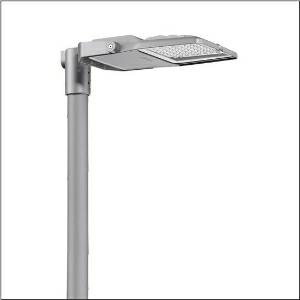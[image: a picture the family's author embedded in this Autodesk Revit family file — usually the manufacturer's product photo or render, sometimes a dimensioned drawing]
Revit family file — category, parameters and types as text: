
# Revit family: floodlight_fl_21_mini___pl33t_5xa7772b4f3a_78ab
name_source: partatom
category: Lighting Fixtures
units: mm (PartAtom-declared; Revit-internal decimal feet)

## family parameters
Cut with Voids When Loaded = No
Host = Face
Light Source = No
Part Type = Normal
Room Calculation Point = No
Round Connector Dimension = Use Diameter
Shared = No

## types (1)
- --- (1 x LED, 6420 lm, 45.5 W, 4000K)
    Apparent Load = 46 VA
    CIE Flux Codes = 26 75 99 100 100
    Color Rendering = 70
    Color Temperature = 4000K
    Default Elevation = 1800 mm
    Description = Floodlight FL 21 mini, floodlight, primary light control with lens, of PMMA, primary optical cover: protective disc, of toughened safety glass, transparent, light distribution: PL33T, light emission: direct distribution, installation type: surface-mounted, LED, High Power LED, rated luminous flux: 6.420lm, luminous efficacy: 141lm/W, light colour: 740, colour temperature: 4000K, control gear: ECG iQ, control: Auto-Match, Temp-Guard, Night-Set, Smart-Wire, Desk-Remote (wireless, voltage-free reading and setting of iQ features in the workshop via application-optimized NFC function/RFID function), optimised constant luminous flux control (CLO 2.0), Light-Fading, Lumen-Switch, with terminal, 6-pole, mains connection: 220..240V, AC, 50/60Hz, start of lifetime: 46W, end of lifetime: 48W, reduction: 22W, luminaire housing, of diecast aluminium, powder-coated, Siteco® metallic grey (DB 702S), corrosivity category C5 according to DIN EN ISO 12944, mast bracket, of steel, galvanised, powder-coated, protection rating (complete): IP66, insulation class (complete): insulation class II (safety insulation), certification: CE, ENEC, VDE, protection symbol: D, impact resistance: IK08, permissible operating ambient temperature: -40..+40°C, permissible operating ambient temperature for outdoor applications: -40..+50°C, standard: DIN EN 12944, packaging unit: 1 piece

Light Distribution: PL33T
    Height = 70 mm
    Lamp = 1 x LED
    Lamp Light Flux = 6420 lm
    Lamp Power = 45.5 W
    Lamp count = 1
    Length = 485 mm
    Luminous efficacy = 141 lm/W
    Manufacturer = Siteco
    ModVariant = No
    Model = 5XA7772B4F3A
    Number of Poles = 1
    OnlyDefault = Yes
    Power Factor = 1
    Product Name = Floodlight FL 21 mini | PL33T
    Product group = floodlight | pylon top
    ProductGroupID = 6101
    Protection Class = Protection class II
    Protection Degree = IP 66
    RLX_Detail_Level = 1
    RlxData = <blob elided: 100897 chars, md5=ec82bb0f>
    Socket = socket
    Standby Power = 0 W
    System Light Flux = 6420 lm
    System Power = 46 W
    Type Comments = factory setting: luminous flux: 100 % | dim-lin: 254 | 463 mA
    Type Image = l_1007125.jpg
    URL = http://relux.com
    VarID = @adj_059909
    Voltage = 0 V
    Weight = 0.00 kg
    Width = 337 mm

## geometry (parser evidence)
native form markers: Blend x4, Sweep x13
no freeform markers — native parametric forms only
